# Revit family: Wood_Lockers-Salsbury_Industries-12000_Series-3_Wide_Units
name_source: partatom
category: Specialty Equipment
revit_build: Autodesk Revit 2016 (Build: 20150714_1515(x64)
units: mm (PartAtom-declared; Revit-internal decimal feet)

## family parameters
Always vertical = Yes
Cut with Voids When Loaded = No
OmniClass Number = 23.40.00.00
OmniClass Title = Equipment and Furnishings
Part Type = Normal
Room Calculation Point = No
Round Connector Dimension = Use Diameter
Shared = No
Work Plane-Based = No

## types (6) — shared parameters
Assembly Code = C1030310
Base Hardware = Aluminum - Salsbury Finish - Black Satin
Base Primary Materials = Particle Board Industrial Grade - Salsbury Finish - Black Melamine Overlay
Base Secondary Material = Particle Board Industrial Grade - Salsbury Finish - Plain
Crown Molding Height = 4.000"
Door Padding = Door Padding - Salsbury Finish - White
Doors = Solid Oak Doors : Double Tier Door
Hardware = Steel Hinge - Salsbury Finish - Chrome
Height = 72.000"
Individual Door Height = 35.781"
Lock Material = Stainless Steel - Salsbury Finish - Gold
Manufacturer = Salsbury Industries
MasterFormat Code = 10 51 16
MasterFormat Title = Lockers
OmniClass 23 Number = 23.40.00.00
OmniClass 23 Title = Equipment and Furnishings
Primary Structure Materials = Particle Board Industrial Grade - Salsbury Finish - White Melamine Inlay
Secondary Structure Materials = Particle Board Industrial Grade - Salsbury Finish - Black Melamine Overlay
Type Comments = 16" Wide Solid Oak Executive Wood Lockers - Double Tier
URL = www.lockers.com
Version = 2.0 (05/31/18)
Width = 48.000"

## per-type parameters (varying)
| type | Base | Base Height | Depth | Description |
| 12368 | Solid Oak Locker Bases : Base - 48" W x 18" D | 4.000" | 18.000" | 3 Wide - 6 Feet High - 18 inches Deep - with Base |
| 12368 - without Base | Solid Oak Locker Bases : None | 0.000" | 18.000" | 3 Wide - 6 Feet High - 18 inches Deep - without Base |
| 12361 - without Base | Solid Oak Locker Bases : None | 0.000" | 21.000" | 3 Wide - 6 Feet High - 21 inches Deep - without Base |
| 12361 | Solid Oak Locker Bases : Base - 48" W x 21" D | 4.000" | 21.000" | 3 Wide - 6 Feet High - 21 inches Deep - with Base |
| 12364 | Solid Oak Locker Bases : Base - 48" W x 24" D | 4.000" | 24.000" | 3 Wide - 6 Feet High - 24 inches Deep - with Base |
| 12364 - without Base | Solid Oak Locker Bases : None | 0.000" | 24.000" | 3 Wide - 6 Feet High - 24 inches Deep - without Base |

note: column(s) folded — value = type name in every type: Model

## geometry (parser evidence)
native form markers: Sweep x25
no freeform markers — native parametric forms only
